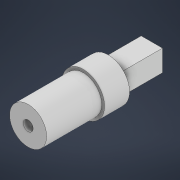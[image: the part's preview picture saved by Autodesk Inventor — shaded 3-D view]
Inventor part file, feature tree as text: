
AUTODESK INVENTOR PART (.ipt)
format: ipt  version: 2021 (Build 250183000, 183)  size: 248,320 bytes
history: native  units: mm
features: extrude x5, sketch x5, other x1
ambient origin geometry x8: Origin, YZ Plane, XZ Plane, XY Plane, X Axis, Y Axis, Z Axis, Center Point
bodies: Volumenkörper1 (feature_tree)
feature tree (11):
  other  "Boogie_Stange"
  extrude  "Extrusion1"  Depth=22.0mm TaperAngle=0.0deg
  extrude  "Extrusion2"  Depth=10.0mm TaperAngle=0.0deg
  extrude  "Extrusion3"  Depth=8.5mm
  extrude  "Extrusion4"  Depth=17.4mm
  extrude  "Extrusion5"  Depth=5.0mm
  sketch  "Skizze1"  dims[d0=14.8mm d1=22.0mm d2=0.0mm]
  sketch  "Skizze2"  dims[d3=17.0mm d4=10.0mm d5=0.0mm]
  sketch  "Skizze3"  dims[d6=8.5mm d7=8.5mm]
  sketch  "Skizze4"  dims[d8=17.4mm d9=0.0mm d10=4.0mm]
  sketch  "Skizze5"  dims[d11=5.0mm d12=0.0mm d13=4.0mm d14=5.0mm d15=0.0mm]
